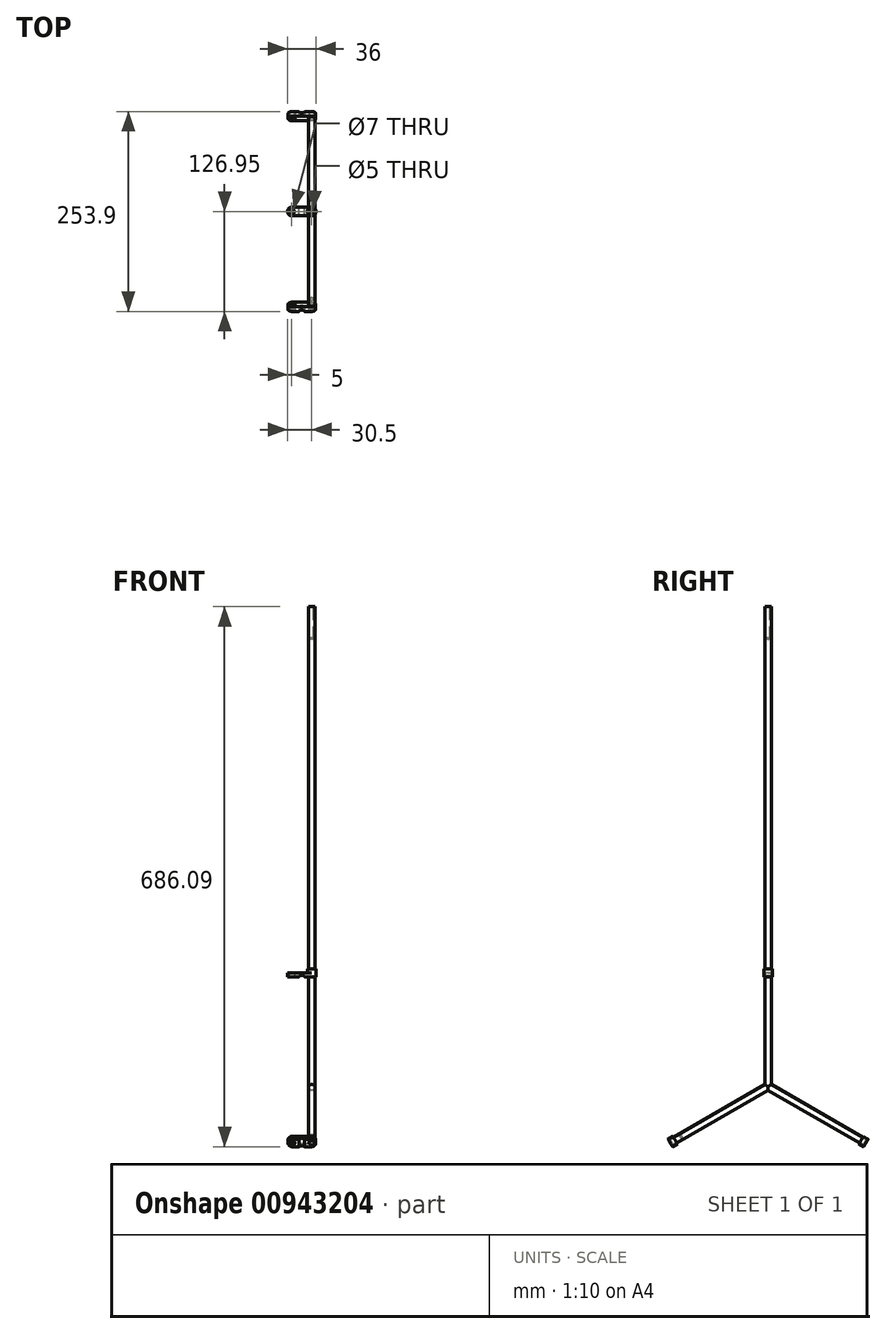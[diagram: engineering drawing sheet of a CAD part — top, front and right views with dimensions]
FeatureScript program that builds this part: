
annotation { "Feature Type Name" : "Feature", "Feature Type Description" : "" }
export const myFeature = defineFeature(function(context is Context, id is Id, definition is map)
    precondition{}
    {
        {
            var Q0;
            Q0=qCreatedBy(makeId("Top.planeOp"),FACE);
            var sketch = newSketch(context, id + "F0", { "sketchPlane" : qUnion([Q0])});
            skCircle(sketch, "E0", {"center": v(0, 0) * mm, "radius": 4.25 * mm});
            skSolve(sketch);
        }
        {
            var Q0;
            Q0=makeQuery(id+"F0.imprint","IMPRINT",FACE,{"disambiguationData":[TD([[makeQuery(id+"F0.imprint","IMPRINT",EDGE,{"derivedFrom":sQuery(id+"F0.wireOp",EDGE,"E0")}),1.0]])]});
            extrude(context, id + "F1", {"entities" : qUnion([Q0]), "depth" : 0 * mm, "offsetDistance" : 25 * mm, "hasSecondDirection" : true, "secondDirectionOppositeDirection" : true, "secondDirectionDepth" : 144.34 * mm});
        }
        {
            var Q0;
            Q0=qCreatedBy(makeId("Top.planeOp"),FACE);
            var sketch = newSketch(context, id + "F2", { "sketchPlane" : qUnion([Q0])});
            skLineSegment(sketch, "E1.bottom", {"start": v(-25.5, -5.5) * mm, "end": v(0, -5.5) * mm});
            skLineSegment(sketch, "E1.top", {"start": v(-25.5, 5.5) * mm, "end": v(0, 5.5) * mm});
            skLineSegment(sketch, "E1.left", {"start": v(-30.5, -0.5) * mm, "end": v(-30.5, 0.5) * mm});
            skLineSegment(sketch, "E1.right", {"start": v(5.5, 0) * mm, "end": v(5.5, 0) * mm});
            skPoint(sketch, "E2.visualSharp", {"position": v(-30.5, -5.5) * mm});
            skArc(sketch, "E2.filletArc", {"start": v(-30.5, -0.5) * mm, "mid": v(-29.04, -4.04) * mm, "end": v(-25.5, -5.5) * mm});
            skPoint(sketch, "E3.visualSharp", {"position": v(-30.5, 5.5) * mm});
            skArc(sketch, "E3.filletArc", {"start": v(-25.5, 5.5) * mm, "mid": v(-29.04, 4.04) * mm, "end": v(-30.5, 0.5) * mm});
            skPoint(sketch, "E4.visualSharp", {"position": v(5.5, -5.5) * mm});
            skArc(sketch, "E4.filletArc", {"start": v(0, -5.5) * mm, "mid": v(3.89, -3.89) * mm, "end": v(5.5, 0) * mm});
            skPoint(sketch, "E5.visualSharp", {"position": v(5.5, 5.5) * mm});
            skArc(sketch, "E5.filletArc", {"start": v(5.5, 0) * mm, "mid": v(3.89, 3.89) * mm, "end": v(0, 5.5) * mm});
            skPoint(sketch, "E6", {"position": v(-25, 0) * mm});
            skSolve(sketch);
        }
        {
            var Q0;
            Q0=qSketchRegion(id+"F2",true);
            extrude(context, id + "F3", {"entities" : qUnion([Q0]), "operationType" : NewBodyOperationType.ADD, "oppositeDirection" : true, "depth" : 5 * mm, "offsetDistance" : 25 * mm});
        }
        {
            var Q0;
            Q0=makeQuery(id+"F3.opExtrude","SWEPT_FACE",FACE,{"disambiguationData":[OSD([sQuery(id+"F2.wireOp",EDGE,"E1.top")])]});
            var sketch = newSketch(context, id + "F4", { "sketchPlane" : qUnion([Q0])});
            skArc(sketch, "E7", {"start": v(16.26, -5) * mm, "mid": v(12.63, -2.96) * mm, "end": v(9, -5) * mm});
            skLineSegment(sketch, "E8", {"start": v(16.26, -5) * mm, "end": v(9, -5) * mm});
            skSolve(sketch);
        }
        {
            var Q0;
            Q0=makeQuery(id+"F4.imprint","IMPRINT",FACE,{"disambiguationData":[TD([[makeQuery(id+"F4.imprint","IMPRINT",EDGE,{"derivedFrom":sQuery(id+"F4.wireOp",EDGE,"E7")}),1.0]])]});
            extrude(context, id + "F5", {"entities" : qUnion([Q0]), "operationType" : NewBodyOperationType.REMOVE, "oppositeDirection" : true, "depth" : 25 * mm, "offsetDistance" : 25 * mm});
        }
        {
            var Q0;
            {var subQ0=sQuery(id+"F2.wireOp",EDGE,"E2.filletArc");var subQ1=sQuery(id+"F2.wireOp",EDGE,"E1.left");var subQ2=sQuery(id+"F2.wireOp",EDGE,"E1.top");var subQ3=sQuery(id+"F2.wireOp",EDGE,"E1.bottom");var subQ4=sQuery(id+"F2.wireOp",EDGE,"E3.filletArc");Q0=makeQuery(id+"F5.boolean.opBoolean","SPLIT",FACE,{"disambiguationData":[TD([makeQuery(id+"F3.opExtrude","SWEPT_FACE",FACE,{"disambiguationData":[OSD([subQ1])]})])],"derivedFrom":makeQuery(id+"F3.opExtrude","CAP_FACE",FACE,{"disambiguationData":[OSD([subQ3,subQ2,subQ1,sQuery(id+"F2.wireOp",EDGE,"E1.right"),subQ0,subQ4,sQuery(id+"F2.wireOp",EDGE,"E4.filletArc"),sQuery(id+"F2.wireOp",EDGE,"E5.filletArc")])],"isStart":false})});}
            var sketch = newSketch(context, id + "F6", { "sketchPlane" : qUnion([Q0])});
            skPoint(sketch, "E9", {"position": v(-25.5, 0) * mm});
            skSolve(sketch);
        }
        {
            var Q0;
            Q0=sQuery(id+"F6.wireOp",VERTEX,"E9");
            var Q1;
            Q1=makeQuery(id+"F1.opExtrude","SWEPT_BODY",BODY,{"disambiguationData":[OSD([sQuery(id+"F0.wireOp",EDGE,"E0")])]});
            hole(context, id + "F7", {"style" : HoleStyle.SIMPLE, "endStyle" : HoleEndStyle.THROUGH, "standardTappedOrClearance" : lookupTablePath({ "standard" : "ISO", "engagement" : "75%", "pitch" : "1 mm", "size" : "M8", "type" : "Tapped" }), "standardBlindInLast" : lookupTablePath({ "standard" : "ISO", "engagement" : "75%", "pitch" : "1 mm", "size" : "M8", "type" : "Tapped" }), "holeDiameter" : 7 * mm, "majorDiameter" : 8 * mm, "showTappedDepth" : true, "isTappedThrough" : true, "tappedDepth" : 37 * mm, "tapClearance" : 3, "locations" : qUnion([Q0]), "scope" : qUnion([Q1])});
        }
        {
            var Q0;
            Q0=qCreatedBy(makeId("Right.planeOp"),FACE);
            var sketch = newSketch(context, id + "F8", { "sketchPlane" : qUnion([Q0])});
            skPoint(sketch, "E10", {"position": v(0, -144.34) * mm});
            skLineSegment(sketch, "E11", {"start": v(0, -144.34) * mm, "end": v(6.32, -147.99) * mm});
            skLineSegment(sketch, "E12", {"start": v(6.32, -147.99) * mm, "end": v(0, -144.34) * mm});
            skLineSegment(sketch, "E13", {"start": v(0, -144.34) * mm, "end": v(-5.64, -147.6) * mm});
            skSolve(sketch);
        }
        {
            var Q0;
            Q0=sQuery(id+"F8.wireOp",VERTEX,"E10");
            var Q1;
            Q1=sQuery(id+"F8.wireOp",EDGE,"E12");
            cPlane(context, id + "F9", {"entities" : qUnion([Q0, Q1]), "cplaneType" : CPlaneType.LINE_POINT, "offset" : 25 * mm, "width" : 150 * mm, "height" : 150 * mm});
        }
        {
            var Q0;
            Q0=sQuery(id+"F8.wireOp",EDGE,"E13");
            var Q1;
            Q1=sQuery(id+"F8.wireOp",VERTEX,"E11.start");
            cPlane(context, id + "F10", {"entities" : qUnion([Q0, Q1]), "cplaneType" : CPlaneType.LINE_POINT, "offset" : 25 * mm, "width" : 150 * mm, "height" : 150 * mm});
        }
        {
            var Q0;
            Q0=qCreatedBy(id+"F9.planeOp",FACE);
            var sketch = newSketch(context, id + "F11", { "sketchPlane" : qUnion([Q0])});
            skCircle(sketch, "E14", {"center": v(0, -125) * mm, "radius": 4.25 * mm});
            skSolve(sketch);
        }
        {
            var Q0;
            Q0=qSketchRegion(id+"F11",true);
            extrude(context, id + "F12", {"entities" : qUnion([Q0]), "operationType" : NewBodyOperationType.ADD, "oppositeDirection" : true, "depth" : 143.42 * mm, "offsetDistance" : 25 * mm});
        }
        {
            var Q0;
            Q0=qCreatedBy(id+"F10.planeOp",FACE);
            var sketch = newSketch(context, id + "F13", { "sketchPlane" : qUnion([Q0])});
            skCircle(sketch, "E15", {"center": v(0, -37560.58) * mm, "radius": 42.5 * mm});
            skCircle(sketch, "E16", {"center": v(0, -125) * mm, "radius": 4.2 * mm});
            skSolve(sketch);
        }
        {
            var Q0;
            Q0=qSketchRegion(id+"F13",true);
            extrude(context, id + "F14", {"entities" : qUnion([Q0]), "operationType" : NewBodyOperationType.ADD, "depth" : 143.42 * mm, "offsetDistance" : 25 * mm});
        }
        {
            var Q0;
            Q0=makeQuery(id+"F14.opExtrude","SWEPT_BODY",BODY,{"disambiguationData":[OSD([sQuery(id+"F13.wireOp",EDGE,"E15")])]});
            deleteBodies(context, id + "F15", {"entities" : qUnion([Q0])});
        }
        {
            var Q0;
            Q0=makeQuery(id+"F12.opExtrude","CAP_FACE",FACE,{"disambiguationData":[OSD([sQuery(id+"F11.wireOp",EDGE,"E14")])],"isStart":false});
            var sketch = newSketch(context, id + "F16", { "sketchPlane" : qUnion([Q0])});
            skLineSegment(sketch, "E17.bottom", {"start": v(0, -119.5) * mm, "end": v(25, -119.5) * mm});
            skLineSegment(sketch, "E17.top", {"start": v(0, -130.5) * mm, "end": v(25, -130.5) * mm});
            skLineSegment(sketch, "E17.left", {"start": v(-5, -124.5) * mm, "end": v(-5, -125.5) * mm});
            skLineSegment(sketch, "E17.right", {"start": v(30, -124.5) * mm, "end": v(30, -125.5) * mm});
            skPoint(sketch, "E18", {"position": v(0, -125) * mm});
            skPoint(sketch, "E19", {"position": v(25, -125) * mm});
            skPoint(sketch, "E20.visualSharp", {"position": v(-5, -119.5) * mm});
            skArc(sketch, "E20.filletArc", {"start": v(0, -119.5) * mm, "mid": v(-3.54, -120.96) * mm, "end": v(-5, -124.5) * mm});
            skPoint(sketch, "E21.visualSharp", {"position": v(30, -119.5) * mm});
            skArc(sketch, "E21.filletArc", {"start": v(30, -124.5) * mm, "mid": v(28.54, -120.96) * mm, "end": v(25, -119.5) * mm});
            skPoint(sketch, "E22.visualSharp", {"position": v(30, -130.5) * mm});
            skArc(sketch, "E22.filletArc", {"start": v(25, -130.5) * mm, "mid": v(28.54, -129.04) * mm, "end": v(30, -125.5) * mm});
            skPoint(sketch, "E23.visualSharp", {"position": v(-5, -130.5) * mm});
            skArc(sketch, "E23.filletArc", {"start": v(-5, -125.5) * mm, "mid": v(-3.54, -129.04) * mm, "end": v(0, -130.5) * mm});
            skSolve(sketch);
        }
        {
            var Q0;
            Q0=qSketchRegion(id+"F16",true);
            extrude(context, id + "F17", {"entities" : qUnion([Q0]), "operationType" : NewBodyOperationType.ADD, "oppositeDirection" : true, "depth" : 7 * mm, "offsetDistance" : 25 * mm});
        }
        {
            var Q0;
            Q0=makeQuery(id+"F17.opExtrude","SWEPT_FACE",FACE,{"disambiguationData":[OSD([sQuery(id+"F16.wireOp",EDGE,"E17.top")])]});
            var sketch = newSketch(context, id + "F18", { "sketchPlane" : qUnion([Q0])});
            skArc(sketch, "E24", {"start": v(-9, -215.59) * mm, "mid": v(-12.63, -213.55) * mm, "end": v(-16.26, -215.59) * mm});
            skSolve(sketch);
        }
        {
            var Q0;
            {var subQ0=sQuery(id+"F18.wireOp",EDGE,"E24");Q0=makeQuery(id+"F18.imprint","IMPRINT",FACE,{"disambiguationData":[TD([[makeQuery(id+"F18.imprint","IMPRINT",EDGE,{"derivedFrom":subQ0}),1.0]])]});}
            extrude(context, id + "F19", {"entities" : qUnion([Q0]), "operationType" : NewBodyOperationType.REMOVE, "oppositeDirection" : true, "depth" : 25 * mm, "offsetDistance" : 25 * mm});
        }
        {
            var Q0;
            {var subQ0=sQuery(id+"F16.wireOp",EDGE,"E20.filletArc");var subQ1=sQuery(id+"F16.wireOp",EDGE,"E17.left");var subQ2=sQuery(id+"F16.wireOp",EDGE,"E17.top");var subQ3=sQuery(id+"F16.wireOp",EDGE,"E17.bottom");var subQ4=sQuery(id+"F16.wireOp",EDGE,"E23.filletArc");Q0=makeQuery(id+"F19.boolean.opBoolean","SPLIT",FACE,{"disambiguationData":[TD([makeQuery(id+"F17.opExtrude","SWEPT_FACE",FACE,{"disambiguationData":[OSD([subQ1])]})])],"derivedFrom":makeQuery(id+"F17.opExtrude","CAP_FACE",FACE,{"disambiguationData":[OSD([subQ3,subQ2,subQ1,sQuery(id+"F16.wireOp",EDGE,"E17.right"),subQ0,sQuery(id+"F16.wireOp",EDGE,"E21.filletArc"),sQuery(id+"F16.wireOp",EDGE,"E22.filletArc"),subQ4])],"isStart":false})});}
            var sketch = newSketch(context, id + "F20", { "sketchPlane" : qUnion([Q0])});
            skPoint(sketch, "E25", {"position": v(0, -125) * mm});
            skPoint(sketch, "E26", {"position": v(25.46, -225.76) * mm});
            skPoint(sketch, "E27", {"position": v(-25, -125) * mm});
            skSolve(sketch);
        }
        {
            var Q0;
            Q0=sQuery(id+"F20.wireOp",VERTEX,"E25");
            var Q1;
            Q1=sQuery(id+"F20.wireOp",VERTEX,"E27");
            var Q2;
            Q2=makeQuery(id+"F1.opExtrude","SWEPT_BODY",BODY,{"disambiguationData":[OSD([sQuery(id+"F0.wireOp",EDGE,"E0")])]});
            hole(context, id + "F21", {"style" : HoleStyle.SIMPLE, "endStyle" : HoleEndStyle.BLIND, "standardTappedOrClearance" : lookupTablePath({ "standard" : "ISO", "engagement" : "75%", "pitch" : "1 mm", "size" : "M8", "type" : "Tapped" }), "standardBlindInLast" : lookupTablePath({ "standard" : "ISO", "engagement" : "75%", "pitch" : "1 mm", "size" : "M8", "type" : "Tapped" }), "holeDiameter" : 7 * mm, "majorDiameter" : 8 * mm, "showTappedDepth" : true, "holeDepth" : 15 * mm, "isTappedThrough" : true, "tappedDepth" : 12 * mm, "tapClearance" : 3, "locations" : qUnion([Q0, Q1]), "scope" : qUnion([Q2])});
        }
        {
            var Q0;
            Q0=makeQuery(id+"F14.opExtrude","CAP_FACE",FACE,{"disambiguationData":[OSD([sQuery(id+"F13.wireOp",EDGE,"E16")])],"isStart":false});
            var sketch = newSketch(context, id + "F22", { "sketchPlane" : qUnion([Q0])});
            skLineSegment(sketch, "E28.bottom", {"start": v(0, -130.5) * mm, "end": v(-25, -130.5) * mm});
            skLineSegment(sketch, "E28.top", {"start": v(0, -119.5) * mm, "end": v(-25, -119.5) * mm});
            skLineSegment(sketch, "E28.left", {"start": v(5, -125.5) * mm, "end": v(5, -124.5) * mm});
            skLineSegment(sketch, "E28.right", {"start": v(-30, -125.5) * mm, "end": v(-30, -124.5) * mm});
            skPoint(sketch, "E29", {"position": v(0, -125) * mm});
            skPoint(sketch, "E30.visualSharp", {"position": v(5, -130.5) * mm});
            skArc(sketch, "E30.filletArc", {"start": v(0, -130.5) * mm, "mid": v(3.54, -129.04) * mm, "end": v(5, -125.5) * mm});
            skPoint(sketch, "E31.visualSharp", {"position": v(5, -119.5) * mm});
            skArc(sketch, "E31.filletArc", {"start": v(5, -124.5) * mm, "mid": v(3.54, -120.96) * mm, "end": v(0, -119.5) * mm});
            skPoint(sketch, "E32.visualSharp", {"position": v(-30, -119.5) * mm});
            skArc(sketch, "E32.filletArc", {"start": v(-25, -119.5) * mm, "mid": v(-28.54, -120.96) * mm, "end": v(-30, -124.5) * mm});
            skPoint(sketch, "E33.visualSharp", {"position": v(-30, -130.5) * mm});
            skArc(sketch, "E33.filletArc", {"start": v(-30, -125.5) * mm, "mid": v(-28.54, -129.04) * mm, "end": v(-25, -130.5) * mm});
            skSolve(sketch);
        }
        {
            var Q0;
            Q0=makeQuery(id+"F22.imprint","IMPRINT",FACE,{"disambiguationData":[TD([[makeQuery(id+"F22.imprint","IMPRINT",EDGE,{"derivedFrom":sQuery(id+"F22.wireOp",EDGE,"E28.bottom")}),-1.0]])]});
            extrude(context, id + "F23", {"entities" : qUnion([Q0]), "operationType" : NewBodyOperationType.ADD, "oppositeDirection" : true, "depth" : 7 * mm, "offsetDistance" : 25 * mm});
        }
        {
            var Q0;
            Q0=makeQuery(id+"F23.opExtrude","SWEPT_FACE",FACE,{"disambiguationData":[OSD([sQuery(id+"F22.wireOp",EDGE,"E28.top")])]});
            var sketch = newSketch(context, id + "F24", { "sketchPlane" : qUnion([Q0])});
            skArc(sketch, "E34", {"start": v(-9, -215.59) * mm, "mid": v(-12.63, -213.55) * mm, "end": v(-16.26, -215.59) * mm});
            skLineSegment(sketch, "E35", {"start": v(-9, -215.59) * mm, "end": v(-16.26, -215.59) * mm});
            skSolve(sketch);
        }
        {
            var Q0;
            Q0=qSketchRegion(id+"F24",true);
            extrude(context, id + "F25", {"entities" : qUnion([Q0]), "operationType" : NewBodyOperationType.REMOVE, "oppositeDirection" : true, "depth" : 25 * mm, "offsetDistance" : 25 * mm});
        }
        {
            var Q0;
            {var subQ0=sQuery(id+"F22.wireOp",EDGE,"E32.filletArc");var subQ1=sQuery(id+"F22.wireOp",EDGE,"E28.top");var subQ2=sQuery(id+"F22.wireOp",EDGE,"E28.right");var subQ3=sQuery(id+"F22.wireOp",EDGE,"E28.bottom");var subQ4=sQuery(id+"F22.wireOp",EDGE,"E33.filletArc");var subQ5=sQuery(id+"F13.wireOp",EDGE,"E16");Q0=makeQuery(id+"F25.boolean.opBoolean","SPLIT",FACE,{"disambiguationData":[TD([makeQuery(id+"F23.opExtrude","SWEPT_FACE",FACE,{"disambiguationData":[OSD([subQ2])]})])],"derivedFrom":makeQuery(id+"F23.boolean.opBoolean","MERGE",FACE,{"derivedFrom":[makeQuery(id+"F14.opExtrude","CAP_FACE",FACE,{"disambiguationData":[OSD([subQ5])],"isStart":false}),makeQuery(id+"F23.opExtrude","CAP_FACE",FACE,{"disambiguationData":[OSD([subQ5,subQ3,subQ1,sQuery(id+"F22.wireOp",EDGE,"E28.left"),subQ2,sQuery(id+"F22.wireOp",EDGE,"E30.filletArc"),sQuery(id+"F22.wireOp",EDGE,"E31.filletArc"),subQ0,subQ4])],"isStart":true})]})});}
            var sketch = newSketch(context, id + "F26", { "sketchPlane" : qUnion([Q0])});
            skPoint(sketch, "E36", {"position": v(0, -125) * mm});
            skPoint(sketch, "E37", {"position": v(-25, -125) * mm});
            skSolve(sketch);
        }
        {
            var Q0;
            Q0=sQuery(id+"F26.wireOp",VERTEX,"E36");
            var Q1;
            Q1=sQuery(id+"F26.wireOp",VERTEX,"E37");
            var Q2;
            Q2=makeQuery(id+"F1.opExtrude","SWEPT_BODY",BODY,{"disambiguationData":[OSD([sQuery(id+"F0.wireOp",EDGE,"E0")])]});
            hole(context, id + "F27", {"style" : HoleStyle.SIMPLE, "endStyle" : HoleEndStyle.BLIND, "standardTappedOrClearance" : lookupTablePath({ "standard" : "ISO", "engagement" : "75%", "pitch" : "1 mm", "size" : "M8", "type" : "Tapped" }), "standardBlindInLast" : lookupTablePath({ "standard" : "ISO", "engagement" : "75%", "pitch" : "1 mm", "size" : "M8", "type" : "Tapped" }), "holeDiameter" : 7 * mm, "majorDiameter" : 8 * mm, "showTappedDepth" : true, "holeDepth" : 15 * mm, "isTappedThrough" : true, "tappedDepth" : 12 * mm, "tapClearance" : 3, "locations" : qUnion([Q0, Q1]), "scope" : qUnion([Q2])});
        }
        {
            var Q0;
            Q0=makeQuery(id+"F3.boolean.opBoolean","MERGE",FACE,{"derivedFrom":[makeQuery(id+"F1.opExtrude","CAP_FACE",FACE,{"disambiguationData":[OSD([sQuery(id+"F0.wireOp",EDGE,"E0")])],"isStart":false}),makeQuery(id+"F3.opExtrude","CAP_FACE",FACE,{"disambiguationData":[OSD([sQuery(id+"F2.wireOp",EDGE,"E1.bottom"),sQuery(id+"F2.wireOp",EDGE,"E1.top"),sQuery(id+"F2.wireOp",EDGE,"E1.left"),sQuery(id+"F2.wireOp",EDGE,"E1.right"),sQuery(id+"F2.wireOp",EDGE,"E2.filletArc"),sQuery(id+"F2.wireOp",EDGE,"E3.filletArc"),sQuery(id+"F2.wireOp",EDGE,"E4.filletArc"),sQuery(id+"F2.wireOp",EDGE,"E5.filletArc")])],"isStart":true})]});
            var sketch = newSketch(context, id + "F28", { "sketchPlane" : qUnion([Q0])});
            skCircle(sketch, "E38", {"center": v(0, 0) * mm, "radius": 5.5 * mm});
            skCircle(sketch, "E39", {"center": v(0, 0) * mm, "radius": 4.25 * mm});
            skSolve(sketch);
        }
        {
            var Q0;
            Q0=makeQuery(id+"F28.imprint","IMPRINT",FACE,{"disambiguationData":[TD([[makeQuery(id+"F28.imprint","IMPRINT",EDGE,{"derivedFrom":sQuery(id+"F28.wireOp",EDGE,"E39")}),-1.0]])]});
            extrude(context, id + "F29", {"entities" : qUnion([Q0]), "operationType" : NewBodyOperationType.ADD, "depth" : 5 * mm, "offsetDistance" : 25 * mm});
        }
        {
            var Q0;
            Q0=makeQuery(id+"F29.boolean.opBoolean","SPLIT",FACE,{"disambiguationData":[TD([makeQuery(id+"F29.opExtrude","SWEPT_FACE",FACE,{"disambiguationData":[OSD([sQuery(id+"F28.wireOp",EDGE,"E39")])]})])],"derivedFrom":makeQuery(id+"F3.boolean.opBoolean","MERGE",FACE,{"derivedFrom":[makeQuery(id+"F1.opExtrude","CAP_FACE",FACE,{"disambiguationData":[OSD([sQuery(id+"F0.wireOp",EDGE,"E0")])],"isStart":false}),makeQuery(id+"F3.opExtrude","CAP_FACE",FACE,{"disambiguationData":[OSD([sQuery(id+"F2.wireOp",EDGE,"E1.bottom"),sQuery(id+"F2.wireOp",EDGE,"E1.top"),sQuery(id+"F2.wireOp",EDGE,"E1.left"),sQuery(id+"F2.wireOp",EDGE,"E2.filletArc"),sQuery(id+"F2.wireOp",EDGE,"E3.filletArc"),sQuery(id+"F2.wireOp",EDGE,"E4.filletArc"),sQuery(id+"F2.wireOp",EDGE,"E5.filletArc")])],"isStart":true})]})});
            extrude(context, id + "F30", {"entities" : qUnion([Q0]), "operationType" : NewBodyOperationType.ADD, "depth" : 465.28 * mm, "offsetDistance" : 25 * mm});
        }
        {
            var Q0;
            Q0=makeQuery(id+"F30.opExtrude","CAP_FACE",FACE,{"disambiguationData":[OSD([sQuery(id+"F0.wireOp",EDGE,"E0"),sQuery(id+"F2.wireOp",EDGE,"E1.bottom"),sQuery(id+"F2.wireOp",EDGE,"E1.top"),sQuery(id+"F2.wireOp",EDGE,"E1.left"),sQuery(id+"F2.wireOp",EDGE,"E2.filletArc"),sQuery(id+"F2.wireOp",EDGE,"E3.filletArc"),sQuery(id+"F2.wireOp",EDGE,"E4.filletArc"),sQuery(id+"F2.wireOp",EDGE,"E5.filletArc")])],"isStart":false});
            var sketch = newSketch(context, id + "F31", { "sketchPlane" : qUnion([Q0])});
            skPoint(sketch, "E40", {"position": v(0, 0) * mm});
            skSolve(sketch);
        }
        {
            var Q0;
            Q0=sQuery(id+"F31.wireOp",VERTEX,"E40");
            var Q1;
            Q1=makeQuery(id+"F1.opExtrude","SWEPT_BODY",BODY,{"disambiguationData":[OSD([sQuery(id+"F0.wireOp",EDGE,"E0")])]});
            hole(context, id + "F32", {"style" : HoleStyle.SIMPLE, "endStyle" : HoleEndStyle.BLIND, "standardTappedOrClearance" : lookupTablePath({ "standard" : "ISO", "engagement" : "75%", "pitch" : "1 mm", "size" : "M6", "type" : "Tapped" }), "standardBlindInLast" : lookupTablePath({ "standard" : "ISO", "engagement" : "75%", "pitch" : "1 mm", "size" : "M6", "type" : "Tapped" }), "holeDiameter" : 5 * mm, "majorDiameter" : 6 * mm, "showTappedDepth" : true, "holeDepth" : 40 * mm, "isTappedThrough" : true, "tappedDepth" : 37 * mm, "tapClearance" : 3, "locations" : qUnion([Q0]), "scope" : qUnion([Q1])});
        }
    });
